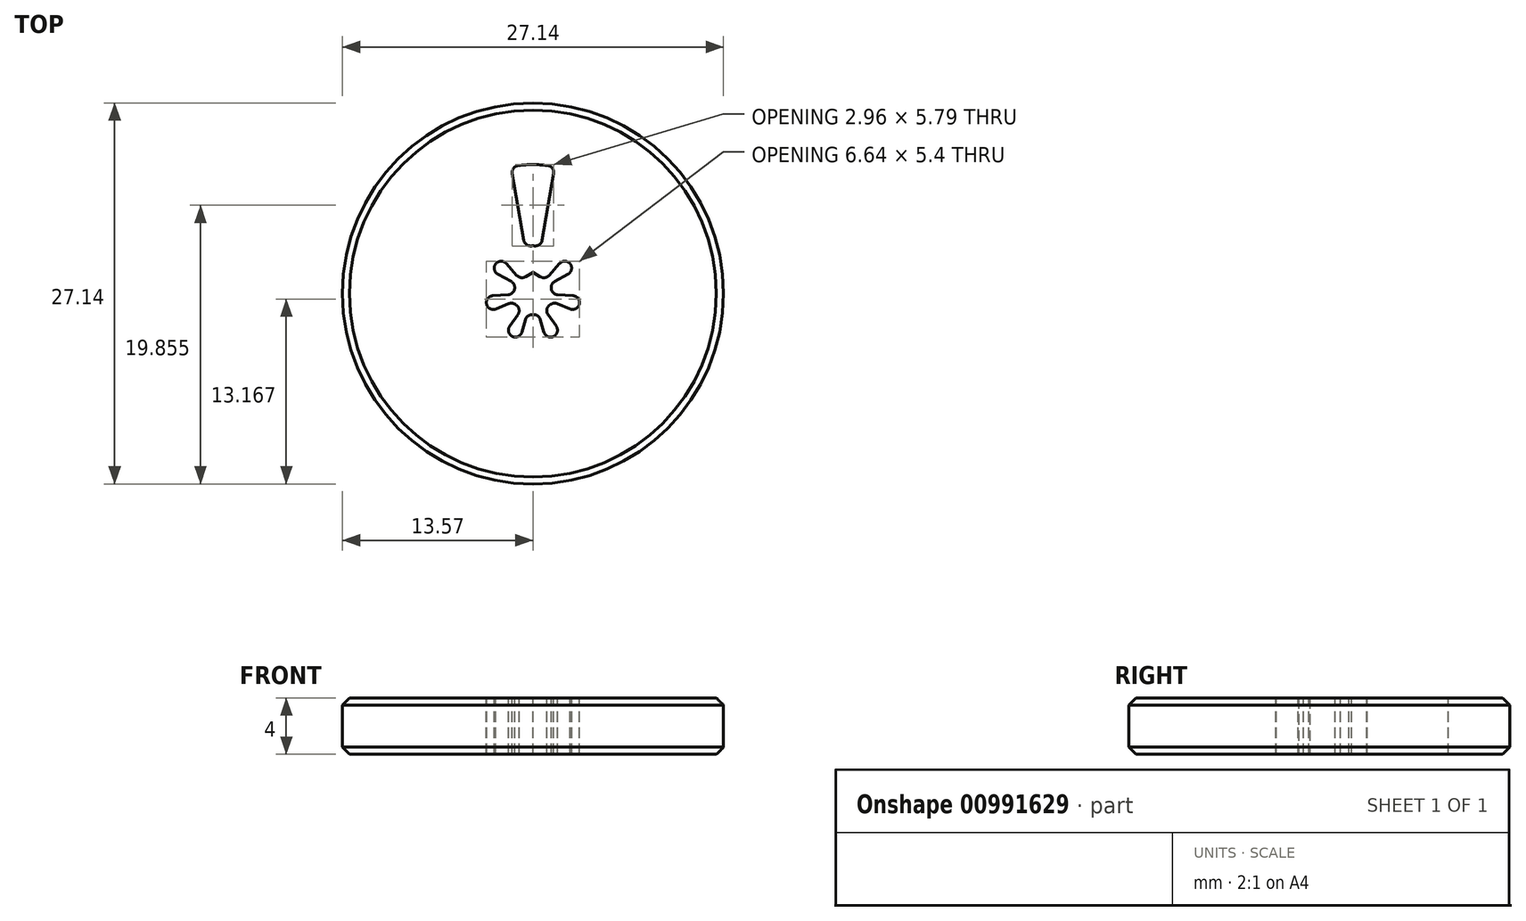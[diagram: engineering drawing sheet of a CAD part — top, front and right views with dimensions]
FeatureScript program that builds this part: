
annotation { "Feature Type Name" : "Feature", "Feature Type Description" : "" }
export const myFeature = defineFeature(function(context is Context, id is Id, definition is map)
    precondition{}
    {
        {
            var Q0;
            Q0=qCreatedBy(makeId("Top.planeOp"),FACE);
            var sketch = newSketch(context, id + "F0", { "sketchPlane" : qUnion([Q0])});
            skCircle(sketch, "E0", {"center": v(0, 0) * mm, "radius": 13.57 * mm});
            skSolve(sketch);
        }
        {
            var Q0;
            Q0=makeQuery(id+"F0.imprint","IMPRINT",FACE,{"disambiguationData":[TD([[makeQuery(id+"F0.imprint","IMPRINT",EDGE,{"derivedFrom":sQuery(id+"F0.wireOp",EDGE,"E0")}),1.0]])]});
            extrude(context, id + "F1", {"entities" : qUnion([Q0]), "endBound" : BoundingType.SYMMETRIC, "depth" : 34 * mm, "offsetDistance" : 25 * mm});
        }
        {
            var Q0;
            Q0=qCreatedBy(makeId("Top.planeOp"),FACE);
            var sketch = newSketch(context, id + "F2", { "sketchPlane" : qUnion([Q0])});
            skPoint(sketch, "E1", {"position": v(0, 17.57) * mm});
            skPoint(sketch, "E2", {"position": v(15.3, 12.2) * mm});
            skPoint(sketch, "E3", {"position": v(19.08, -4.36) * mm});
            skPoint(sketch, "E4", {"position": v(8.5, -17.64) * mm});
            skPoint(sketch, "E5", {"position": v(-8.5, -17.64) * mm});
            skPoint(sketch, "E6", {"position": v(-19.08, -4.36) * mm});
            skPoint(sketch, "E7", {"position": v(-15.3, 12.2) * mm});
            skArc(sketch, "E8", {"start": v(-1, 17.55) * mm, "mid": v(0, 17.57) * mm, "end": v(1, 17.55) * mm});
            skPoint(sketch, "E9", {"position": v(-12.18, 9.71) * mm});
            skPoint(sketch, "E10", {"position": v(12.18, 9.71) * mm});
            skPoint(sketch, "E11", {"position": v(15.18, -3.47) * mm});
            skPoint(sketch, "E12", {"position": v(6.76, -14.03) * mm});
            skPoint(sketch, "E13", {"position": v(-6.76, -14.03) * mm});
            skPoint(sketch, "E14", {"position": v(-15.18, -3.47) * mm});
            skPoint(sketch, "E15", {"position": v(0, 13.57) * mm});
            skArc(sketch, "E16", {"start": v(-2.5, 13.34) * mm, "mid": v(0, 13.57) * mm, "end": v(2.5, 13.34) * mm});
            skLineSegment(sketch, "E17", {"start": v(-2.5, 13.34) * mm, "end": v(-1, 17.55) * mm});
            skLineSegment(sketch, "E18", {"start": v(1, 17.55) * mm, "end": v(2.5, 13.34) * mm});
            skLineSegment(sketch, "E19.1.0", {"start": v(14.34, 10.16) * mm, "end": v(11.99, 6.36) * mm});
            skArc(sketch, "E19.1.1", {"start": v(8.87, 10.27) * mm, "mid": v(10.61, 8.46) * mm, "end": v(11.99, 6.36) * mm});
            skLineSegment(sketch, "E19.1.2", {"start": v(8.87, 10.27) * mm, "end": v(13.1, 11.72) * mm});
            skArc(sketch, "E19.1.3", {"start": v(13.1, 11.72) * mm, "mid": v(13.74, 10.96) * mm, "end": v(14.34, 10.16) * mm});
            skLineSegment(sketch, "E19.2.0", {"start": v(16.88, -4.88) * mm, "end": v(12.45, -5.4) * mm});
            skArc(sketch, "E19.2.1", {"start": v(13.56, -0.53) * mm, "mid": v(13.23, -3.02) * mm, "end": v(12.45, -5.4) * mm});
            skLineSegment(sketch, "E19.2.2", {"start": v(13.56, -0.53) * mm, "end": v(17.33, -2.93) * mm});
            skArc(sketch, "E19.2.3", {"start": v(17.33, -2.93) * mm, "mid": v(17.13, -3.91) * mm, "end": v(16.88, -4.88) * mm});
            skLineSegment(sketch, "E19.3.0", {"start": v(6.71, -16.24) * mm, "end": v(3.54, -13.1) * mm});
            skArc(sketch, "E19.3.1", {"start": v(8.04, -10.94) * mm, "mid": v(5.89, -12.23) * mm, "end": v(3.54, -13.1) * mm});
            skLineSegment(sketch, "E19.3.2", {"start": v(8.04, -10.94) * mm, "end": v(8.51, -15.37) * mm});
            skArc(sketch, "E19.3.3", {"start": v(8.51, -15.37) * mm, "mid": v(7.63, -15.83) * mm, "end": v(6.71, -16.24) * mm});
            skLineSegment(sketch, "E19.4.0", {"start": v(-8.51, -15.37) * mm, "end": v(-8.04, -10.94) * mm});
            skArc(sketch, "E19.4.1", {"start": v(-3.54, -13.1) * mm, "mid": v(-5.89, -12.23) * mm, "end": v(-8.04, -10.94) * mm});
            skLineSegment(sketch, "E19.4.2", {"start": v(-3.54, -13.1) * mm, "end": v(-6.71, -16.24) * mm});
            skArc(sketch, "E19.4.3", {"start": v(-6.71, -16.24) * mm, "mid": v(-7.63, -15.83) * mm, "end": v(-8.51, -15.37) * mm});
            skLineSegment(sketch, "E19.5.0", {"start": v(-17.33, -2.93) * mm, "end": v(-13.56, -0.53) * mm});
            skArc(sketch, "E19.5.1", {"start": v(-12.45, -5.4) * mm, "mid": v(-13.23, -3.02) * mm, "end": v(-13.56, -0.53) * mm});
            skLineSegment(sketch, "E19.5.2", {"start": v(-12.45, -5.4) * mm, "end": v(-16.88, -4.88) * mm});
            skArc(sketch, "E19.5.3", {"start": v(-16.88, -4.88) * mm, "mid": v(-17.13, -3.91) * mm, "end": v(-17.33, -2.93) * mm});
            skLineSegment(sketch, "E19.6.0", {"start": v(-13.1, 11.72) * mm, "end": v(-8.87, 10.27) * mm});
            skArc(sketch, "E19.6.1", {"start": v(-11.99, 6.36) * mm, "mid": v(-10.61, 8.46) * mm, "end": v(-8.87, 10.27) * mm});
            skLineSegment(sketch, "E19.6.2", {"start": v(-11.99, 6.36) * mm, "end": v(-14.34, 10.16) * mm});
            skArc(sketch, "E19.6.3", {"start": v(-14.34, 10.16) * mm, "mid": v(-13.74, 10.96) * mm, "end": v(-13.1, 11.72) * mm});
            skLineSegment(sketch, "E19.anchor1", {"start": v(0, 0) * mm, "end": v(2.5, 13.34) * mm, "construction": true});
            skLineSegment(sketch, "E19.anchor2", {"start": v(0, 0) * mm, "end": v(-8.87, 10.27) * mm, "construction": true});
            skSolve(sketch);
        }
        {
            var Q0;
            Q0=makeQuery(id+"F2.imprint","IMPRINT",FACE,{"disambiguationData":[TD([[makeQuery(id+"F2.imprint","IMPRINT",EDGE,{"derivedFrom":sQuery(id+"F2.wireOp",EDGE,"E19.6.0")}),-1.0]])]});
            var Q1;
            Q1=makeQuery(id+"F2.imprint","IMPRINT",FACE,{"disambiguationData":[TD([[makeQuery(id+"F2.imprint","IMPRINT",EDGE,{"derivedFrom":sQuery(id+"F2.wireOp",EDGE,"E8")}),-1.0]])]});
            var Q2;
            Q2=makeQuery(id+"F2.imprint","IMPRINT",FACE,{"disambiguationData":[TD([[makeQuery(id+"F2.imprint","IMPRINT",EDGE,{"derivedFrom":sQuery(id+"F2.wireOp",EDGE,"E19.1.0")}),-1.0]])]});
            var Q3;
            Q3=makeQuery(id+"F2.imprint","IMPRINT",FACE,{"disambiguationData":[TD([[makeQuery(id+"F2.imprint","IMPRINT",EDGE,{"derivedFrom":sQuery(id+"F2.wireOp",EDGE,"E19.2.0")}),-1.0]])]});
            var Q4;
            Q4=makeQuery(id+"F2.imprint","IMPRINT",FACE,{"disambiguationData":[TD([[makeQuery(id+"F2.imprint","IMPRINT",EDGE,{"derivedFrom":sQuery(id+"F2.wireOp",EDGE,"E19.3.0")}),-1.0]])]});
            var Q5;
            Q5=makeQuery(id+"F2.imprint","IMPRINT",FACE,{"disambiguationData":[TD([[makeQuery(id+"F2.imprint","IMPRINT",EDGE,{"derivedFrom":sQuery(id+"F2.wireOp",EDGE,"E19.4.0")}),-1.0]])]});
            var Q6;
            Q6=makeQuery(id+"F2.imprint","IMPRINT",FACE,{"disambiguationData":[TD([[makeQuery(id+"F2.imprint","IMPRINT",EDGE,{"derivedFrom":sQuery(id+"F2.wireOp",EDGE,"E19.5.0")}),-1.0]])]});
            extrude(context, id + "F3", {"entities" : qUnion([Q0, Q1, Q2, Q3, Q4, Q5, Q6]), "operationType" : NewBodyOperationType.ADD, "endBound" : BoundingType.SYMMETRIC, "depth" : 3 * mm, "offsetDistance" : 25 * mm});
        }
        {
            var Q0;
            Q0=makeQuery(id+"F1.opExtrude","CAP_FACE",FACE,{"disambiguationData":[OSD([sQuery(id+"F0.wireOp",EDGE,"E0")])],"isStart":false});
            var sketch = newSketch(context, id + "F4", { "sketchPlane" : qUnion([Q0])});
            skLineSegment(sketch, "E20", {"start": v(0, 0) * mm, "end": v(0, 3.4) * mm});
            skLineSegment(sketch, "E21", {"start": v(0, 3.4) * mm, "end": v(0, 6.79) * mm});
            skLineSegment(sketch, "E22", {"start": v(0, 10.18) * mm, "end": v(0, 13.57) * mm});
            skArc(sketch, "E23", {"start": v(-0.58, 3.34) * mm, "mid": v(0, 3.4) * mm, "end": v(0.58, 3.34) * mm});
            skPoint(sketch, "E24", {"position": v(0, 3.4) * mm});
            skLineSegment(sketch, "E25", {"start": v(0, 0) * mm, "end": v(-1.56, 9.05) * mm});
            skLineSegment(sketch, "E26", {"start": v(1.56, 9.05) * mm, "end": v(0, 0) * mm});
            skCircle(sketch, "E27.cCircle", {"center": v(0, 0) * mm, "radius": 1.5 * mm, "construction": true});
            skLineSegment(sketch, "E27.0", {"start": v(0, 1.5) * mm, "end": v(1.3, 0.75) * mm});
            skLineSegment(sketch, "E27.1", {"start": v(1.3, 0.75) * mm, "end": v(1.3, -0.75) * mm});
            skLineSegment(sketch, "E27.2", {"start": v(1.3, -0.75) * mm, "end": v(0, -1.5) * mm});
            skLineSegment(sketch, "E27.3", {"start": v(0, -1.5) * mm, "end": v(-1.3, -0.75) * mm});
            skLineSegment(sketch, "E27.4", {"start": v(-1.3, -0.75) * mm, "end": v(-1.3, 0.75) * mm});
            skLineSegment(sketch, "E27.5", {"start": v(-1.3, 0.75) * mm, "end": v(0, 1.5) * mm});
            skArc(sketch, "E28", {"start": v(-1.56, 9.05) * mm, "mid": v(0, 9.18) * mm, "end": v(1.56, 9.05) * mm});
            skLineSegment(sketch, "E29", {"start": v(0, 6.79) * mm, "end": v(0, 10.18) * mm});
            skLineSegment(sketch, "E30.1.0", {"start": v(0, 0) * mm, "end": v(-8.05, 4.42) * mm});
            skLineSegment(sketch, "E30.1.1", {"start": v(-6.1, 6.86) * mm, "end": v(0, 0) * mm});
            skArc(sketch, "E30.1.2", {"start": v(-2.97, 1.63) * mm, "mid": v(-2.65, 2.12) * mm, "end": v(-2.25, 2.54) * mm});
            skArc(sketch, "E30.1.3", {"start": v(-8.05, 4.42) * mm, "mid": v(-7.18, 5.72) * mm, "end": v(-6.1, 6.86) * mm});
            skLineSegment(sketch, "E30.2.0", {"start": v(0, 0) * mm, "end": v(-8.47, -3.54) * mm});
            skLineSegment(sketch, "E30.2.1", {"start": v(-9.17, -0.49) * mm, "end": v(0, 0) * mm});
            skArc(sketch, "E30.2.2", {"start": v(-3.13, -1.3) * mm, "mid": v(-3.3, -0.76) * mm, "end": v(-3.39, -0.18) * mm});
            skArc(sketch, "E30.2.3", {"start": v(-8.47, -3.54) * mm, "mid": v(-8.95, -2.04) * mm, "end": v(-9.17, -0.49) * mm});
            skLineSegment(sketch, "E30.3.0", {"start": v(0, 0) * mm, "end": v(-2.52, -8.83) * mm});
            skLineSegment(sketch, "E30.3.1", {"start": v(-5.33, -7.47) * mm, "end": v(0, 0) * mm});
            skArc(sketch, "E30.3.2", {"start": v(-0.93, -3.26) * mm, "mid": v(-1.47, -3.06) * mm, "end": v(-1.97, -2.76) * mm});
            skArc(sketch, "E30.3.3", {"start": v(-2.52, -8.83) * mm, "mid": v(-3.98, -8.27) * mm, "end": v(-5.33, -7.47) * mm});
            skLineSegment(sketch, "E30.4.0", {"start": v(0, 0) * mm, "end": v(5.33, -7.47) * mm});
            skLineSegment(sketch, "E30.4.1", {"start": v(2.52, -8.83) * mm, "end": v(0, 0) * mm});
            skArc(sketch, "E30.4.2", {"start": v(1.97, -2.76) * mm, "mid": v(1.47, -3.06) * mm, "end": v(0.93, -3.26) * mm});
            skArc(sketch, "E30.4.3", {"start": v(5.33, -7.47) * mm, "mid": v(3.98, -8.27) * mm, "end": v(2.52, -8.83) * mm});
            skLineSegment(sketch, "E30.5.0", {"start": v(0, 0) * mm, "end": v(9.17, -0.49) * mm});
            skLineSegment(sketch, "E30.5.1", {"start": v(8.47, -3.54) * mm, "end": v(0, 0) * mm});
            skArc(sketch, "E30.5.2", {"start": v(3.39, -0.18) * mm, "mid": v(3.3, -0.76) * mm, "end": v(3.13, -1.3) * mm});
            skArc(sketch, "E30.5.3", {"start": v(9.17, -0.49) * mm, "mid": v(8.95, -2.04) * mm, "end": v(8.47, -3.54) * mm});
            skLineSegment(sketch, "E30.6.0", {"start": v(0, 0) * mm, "end": v(6.1, 6.86) * mm});
            skLineSegment(sketch, "E30.6.1", {"start": v(8.05, 4.42) * mm, "end": v(0, 0) * mm});
            skArc(sketch, "E30.6.2", {"start": v(2.25, 2.54) * mm, "mid": v(2.65, 2.12) * mm, "end": v(2.97, 1.63) * mm});
            skArc(sketch, "E30.6.3", {"start": v(6.1, 6.86) * mm, "mid": v(7.18, 5.72) * mm, "end": v(8.05, 4.42) * mm});
            skSolve(sketch);
        }
        {
            var Q0;
            {var subQ0=sQuery(id+"F4.wireOp",EDGE,"4e22676c-9bee-4e88-9cae-636ff35edcea.1.0");Q0=makeQuery(id+"F4.imprint","IMPRINT",FACE,{"disambiguationData":[TD([[makeQuery(id+"F4.imprint","IMPRINT",EDGE,{"derivedFrom":subQ0}),-1.0]])]});}
            var Q1;
            {var subQ1=sQuery(id+"F4.wireOp",EDGE,"E21");Q1=makeQuery(id+"F4.imprint","IMPRINT",FACE,{"disambiguationData":[TD([[makeQuery(id+"F4.imprint","IMPRINT",EDGE,{"derivedFrom":subQ1}),1.0]])]});}
            var Q2;
            {var subQ5=sQuery(id+"F4.wireOp",EDGE,"E21");Q2=makeQuery(id+"F4.imprint","IMPRINT",FACE,{"disambiguationData":[TD([[makeQuery(id+"F4.imprint","IMPRINT",EDGE,{"derivedFrom":subQ5}),-1.0]])]});}
            var Q3;
            {var subQ0=sQuery(id+"F4.wireOp",EDGE,"4e22676c-9bee-4e88-9cae-636ff35edcea.6.0");Q3=makeQuery(id+"F4.imprint","IMPRINT",FACE,{"disambiguationData":[TD([[makeQuery(id+"F4.imprint","IMPRINT",EDGE,{"derivedFrom":subQ0}),-1.0]])]});}
            var Q4;
            {var subQ0=sQuery(id+"F4.wireOp",EDGE,"4e22676c-9bee-4e88-9cae-636ff35edcea.5.0");Q4=makeQuery(id+"F4.imprint","IMPRINT",FACE,{"disambiguationData":[TD([[makeQuery(id+"F4.imprint","IMPRINT",EDGE,{"derivedFrom":subQ0}),-1.0]])]});}
            var Q5;
            {var subQ0=sQuery(id+"F4.wireOp",EDGE,"4e22676c-9bee-4e88-9cae-636ff35edcea.4.0");Q5=makeQuery(id+"F4.imprint","IMPRINT",FACE,{"disambiguationData":[TD([[makeQuery(id+"F4.imprint","IMPRINT",EDGE,{"derivedFrom":subQ0}),-1.0]])]});}
            var Q6;
            {var subQ0=sQuery(id+"F4.wireOp",EDGE,"4e22676c-9bee-4e88-9cae-636ff35edcea.3.0");Q6=makeQuery(id+"F4.imprint","IMPRINT",FACE,{"disambiguationData":[TD([[makeQuery(id+"F4.imprint","IMPRINT",EDGE,{"derivedFrom":subQ0}),-1.0]])]});}
            var Q7;
            {var subQ0=sQuery(id+"F4.wireOp",EDGE,"4e22676c-9bee-4e88-9cae-636ff35edcea.2.0");Q7=makeQuery(id+"F4.imprint","IMPRINT",FACE,{"disambiguationData":[TD([[makeQuery(id+"F4.imprint","IMPRINT",EDGE,{"derivedFrom":subQ0}),-1.0]])]});}
            var Q8;
            {var subQ3=sQuery(id+"F4.wireOp",EDGE,"E27.5");var subQ5=sQuery(id+"F4.wireOp",EDGE,"E27.4");var subQ7=makeQuery(id+"F4.imprint","INTERSECT",VERTEX,{"derivedFrom":[subQ5,subQ3]});Q8=makeQuery(id+"F4.imprint","IMPRINT",FACE,{"disambiguationData":[TD([[makeQuery(id+"F4.imprint","IMPRINT",EDGE,{"disambiguationData":[TD([[subQ7,1.0]])],"derivedFrom":subQ5}),-1.0]])]});}
            var Q9;
            {var subQ1=sQuery(id+"F4.wireOp",EDGE,"E25");var subQ3=sQuery(id+"F4.wireOp",EDGE,"E27.5");var subQ4=makeQuery(id+"F4.imprint","INTERSECT",VERTEX,{"derivedFrom":[subQ1,subQ3]});Q9=makeQuery(id+"F4.imprint","IMPRINT",FACE,{"disambiguationData":[TD([[makeQuery(id+"F4.imprint","IMPRINT",EDGE,{"disambiguationData":[TD([[subQ4,1.0]])],"derivedFrom":subQ3}),-1.0]])]});}
            var Q10;
            {var subQ0=sQuery(id+"F4.wireOp",EDGE,"E25");var subQ3=sQuery(id+"F4.wireOp",EDGE,"E27.5");var subQ5=makeQuery(id+"F4.imprint","INTERSECT",VERTEX,{"derivedFrom":[subQ0,subQ3]});Q10=makeQuery(id+"F4.imprint","IMPRINT",FACE,{"disambiguationData":[TD([[makeQuery(id+"F4.imprint","IMPRINT",EDGE,{"disambiguationData":[TD([[subQ5,-1.0]])],"derivedFrom":subQ3}),-1.0]])]});}
            var Q11;
            {var subQ0=sQuery(id+"F4.wireOp",EDGE,"E26");var subQ3=sQuery(id+"F4.wireOp",EDGE,"E27.0");var subQ5=makeQuery(id+"F4.imprint","INTERSECT",VERTEX,{"derivedFrom":[subQ0,subQ3]});Q11=makeQuery(id+"F4.imprint","IMPRINT",FACE,{"disambiguationData":[TD([[makeQuery(id+"F4.imprint","IMPRINT",EDGE,{"disambiguationData":[TD([[subQ5,1.0]])],"derivedFrom":subQ3}),-1.0]])]});}
            var Q12;
            {var subQ1=sQuery(id+"F4.wireOp",EDGE,"E26");var subQ3=sQuery(id+"F4.wireOp",EDGE,"E27.0");var subQ4=makeQuery(id+"F4.imprint","INTERSECT",VERTEX,{"derivedFrom":[subQ1,subQ3]});Q12=makeQuery(id+"F4.imprint","IMPRINT",FACE,{"disambiguationData":[TD([[makeQuery(id+"F4.imprint","IMPRINT",EDGE,{"disambiguationData":[TD([[subQ4,-1.0]])],"derivedFrom":subQ3}),-1.0]])]});}
            var Q13;
            {var subQ3=sQuery(id+"F4.wireOp",EDGE,"E27.1");var subQ5=sQuery(id+"F4.wireOp",EDGE,"E27.0");var subQ7=makeQuery(id+"F4.imprint","INTERSECT",VERTEX,{"derivedFrom":[subQ5,subQ3]});Q13=makeQuery(id+"F4.imprint","IMPRINT",FACE,{"disambiguationData":[TD([[makeQuery(id+"F4.imprint","IMPRINT",EDGE,{"disambiguationData":[TD([[subQ7,1.0]])],"derivedFrom":subQ5}),-1.0]])]});}
            var Q14;
            {var subQ1=sQuery(id+"F4.wireOp",EDGE,"4e22676c-9bee-4e88-9cae-636ff35edcea.5.3");var subQ3=sQuery(id+"F4.wireOp",EDGE,"E27.1");var subQ4=makeQuery(id+"F4.imprint","INTERSECT",VERTEX,{"derivedFrom":[subQ1,subQ3]});Q14=makeQuery(id+"F4.imprint","IMPRINT",FACE,{"disambiguationData":[TD([[makeQuery(id+"F4.imprint","IMPRINT",EDGE,{"disambiguationData":[TD([[subQ4,1.0]])],"derivedFrom":subQ3}),-1.0]])]});}
            var Q15;
            {var subQ1=sQuery(id+"F4.wireOp",EDGE,"4e22676c-9bee-4e88-9cae-636ff35edcea.5.1");var subQ3=sQuery(id+"F4.wireOp",EDGE,"E27.1");var subQ4=makeQuery(id+"F4.imprint","INTERSECT",VERTEX,{"derivedFrom":[subQ1,subQ3]});Q15=makeQuery(id+"F4.imprint","IMPRINT",FACE,{"disambiguationData":[TD([[makeQuery(id+"F4.imprint","IMPRINT",EDGE,{"disambiguationData":[TD([[subQ4,1.0]])],"derivedFrom":subQ3}),-1.0]])]});}
            var Q16;
            {var subQ3=sQuery(id+"F4.wireOp",EDGE,"E27.2");var subQ5=sQuery(id+"F4.wireOp",EDGE,"E27.1");var subQ6=makeQuery(id+"F4.imprint","INTERSECT",VERTEX,{"derivedFrom":[subQ5,subQ3]});Q16=makeQuery(id+"F4.imprint","IMPRINT",FACE,{"disambiguationData":[TD([[makeQuery(id+"F4.imprint","IMPRINT",EDGE,{"disambiguationData":[TD([[subQ6,1.0]])],"derivedFrom":subQ5}),-1.0]])]});}
            var Q17;
            {var subQ1=sQuery(id+"F4.wireOp",EDGE,"4e22676c-9bee-4e88-9cae-636ff35edcea.4.1");var subQ3=sQuery(id+"F4.wireOp",EDGE,"E27.2");var subQ4=makeQuery(id+"F4.imprint","INTERSECT",VERTEX,{"derivedFrom":[subQ1,subQ3]});Q17=makeQuery(id+"F4.imprint","IMPRINT",FACE,{"disambiguationData":[TD([[makeQuery(id+"F4.imprint","IMPRINT",EDGE,{"disambiguationData":[TD([[subQ4,1.0]])],"derivedFrom":subQ3}),-1.0]])]});}
            var Q18;
            {var subQ3=sQuery(id+"F4.wireOp",EDGE,"E27.3");var subQ5=sQuery(id+"F4.wireOp",EDGE,"E27.2");var subQ7=makeQuery(id+"F4.imprint","INTERSECT",VERTEX,{"derivedFrom":[subQ5,subQ3]});Q18=makeQuery(id+"F4.imprint","IMPRINT",FACE,{"disambiguationData":[TD([[makeQuery(id+"F4.imprint","IMPRINT",EDGE,{"disambiguationData":[TD([[subQ7,1.0]])],"derivedFrom":subQ5}),-1.0]])]});}
            var Q19;
            {var subQ1=sQuery(id+"F4.wireOp",EDGE,"4e22676c-9bee-4e88-9cae-636ff35edcea.3.1");var subQ3=sQuery(id+"F4.wireOp",EDGE,"E27.3");var subQ4=makeQuery(id+"F4.imprint","INTERSECT",VERTEX,{"derivedFrom":[subQ1,subQ3]});Q19=makeQuery(id+"F4.imprint","IMPRINT",FACE,{"disambiguationData":[TD([[makeQuery(id+"F4.imprint","IMPRINT",EDGE,{"disambiguationData":[TD([[subQ4,1.0]])],"derivedFrom":subQ3}),-1.0]])]});}
            var Q20;
            {var subQ3=sQuery(id+"F4.wireOp",EDGE,"E27.4");var subQ5=sQuery(id+"F4.wireOp",EDGE,"E27.3");var subQ7=makeQuery(id+"F4.imprint","INTERSECT",VERTEX,{"derivedFrom":[subQ5,subQ3]});Q20=makeQuery(id+"F4.imprint","IMPRINT",FACE,{"disambiguationData":[TD([[makeQuery(id+"F4.imprint","IMPRINT",EDGE,{"disambiguationData":[TD([[subQ7,1.0]])],"derivedFrom":subQ5}),-1.0]])]});}
            var Q21;
            {var subQ1=sQuery(id+"F4.wireOp",EDGE,"4e22676c-9bee-4e88-9cae-636ff35edcea.2.1");var subQ3=sQuery(id+"F4.wireOp",EDGE,"E27.4");var subQ4=makeQuery(id+"F4.imprint","INTERSECT",VERTEX,{"derivedFrom":[subQ1,subQ3]});Q21=makeQuery(id+"F4.imprint","IMPRINT",FACE,{"disambiguationData":[TD([[makeQuery(id+"F4.imprint","IMPRINT",EDGE,{"disambiguationData":[TD([[subQ4,1.0]])],"derivedFrom":subQ3}),-1.0]])]});}
            var Q22;
            {var subQ1=sQuery(id+"F4.wireOp",EDGE,"4e22676c-9bee-4e88-9cae-636ff35edcea.1.3");var subQ3=sQuery(id+"F4.wireOp",EDGE,"E27.4");var subQ4=makeQuery(id+"F4.imprint","INTERSECT",VERTEX,{"derivedFrom":[subQ1,subQ3]});Q22=makeQuery(id+"F4.imprint","IMPRINT",FACE,{"disambiguationData":[TD([[makeQuery(id+"F4.imprint","IMPRINT",EDGE,{"disambiguationData":[TD([[subQ4,1.0]])],"derivedFrom":subQ3}),-1.0]])]});}
            var Q23;
            {var subQ2=sQuery(id+"F4.wireOp",EDGE,"E30.1.2");Q23=makeQuery(id+"F4.imprint","IMPRINT",FACE,{"disambiguationData":[TD([[makeQuery(id+"F4.imprint","IMPRINT",EDGE,{"derivedFrom":subQ2}),1.0]])]});}
            var Q24;
            {var subQ2=sQuery(id+"F4.wireOp",EDGE,"E30.6.2");Q24=makeQuery(id+"F4.imprint","IMPRINT",FACE,{"disambiguationData":[TD([[makeQuery(id+"F4.imprint","IMPRINT",EDGE,{"derivedFrom":subQ2}),1.0]])]});}
            var Q25;
            {var subQ2=sQuery(id+"F4.wireOp",EDGE,"E30.5.2");Q25=makeQuery(id+"F4.imprint","IMPRINT",FACE,{"disambiguationData":[TD([[makeQuery(id+"F4.imprint","IMPRINT",EDGE,{"derivedFrom":subQ2}),1.0]])]});}
            var Q26;
            {var subQ2=sQuery(id+"F4.wireOp",EDGE,"E30.2.2");Q26=makeQuery(id+"F4.imprint","IMPRINT",FACE,{"disambiguationData":[TD([[makeQuery(id+"F4.imprint","IMPRINT",EDGE,{"derivedFrom":subQ2}),1.0]])]});}
            var Q27;
            {var subQ2=sQuery(id+"F4.wireOp",EDGE,"E30.3.2");Q27=makeQuery(id+"F4.imprint","IMPRINT",FACE,{"disambiguationData":[TD([[makeQuery(id+"F4.imprint","IMPRINT",EDGE,{"derivedFrom":subQ2}),1.0]])]});}
            var Q28;
            {var subQ2=sQuery(id+"F4.wireOp",EDGE,"E30.4.2");Q28=makeQuery(id+"F4.imprint","IMPRINT",FACE,{"disambiguationData":[TD([[makeQuery(id+"F4.imprint","IMPRINT",EDGE,{"derivedFrom":subQ2}),1.0]])]});}
            extrude(context, id + "F5", {"entities" : qUnion([Q0, Q1, Q2, Q3, Q4, Q5, Q6, Q7, Q8, Q9, Q10, Q11, Q12, Q13, Q14, Q15, Q16, Q17, Q18, Q19, Q20, Q21, Q22, Q23, Q24, Q25, Q26, Q27, Q28]), "operationType" : NewBodyOperationType.REMOVE, "oppositeDirection" : true, "depth" : 34 * mm, "offsetDistance" : 25 * mm});
        }
        {
            var Q0;
            Q0=makeQuery(id+"F1.opExtrude","CAP_FACE",FACE,{"disambiguationData":[OSD([sQuery(id+"F0.wireOp",EDGE,"E0")])],"isStart":true});
            var sketch = newSketch(context, id + "F6", { "sketchPlane" : qUnion([Q0])});
            skCircle(sketch, "E31", {"center": v(0, 0) * mm, "radius": 13.57 * mm});
            skCircle(sketch, "E32", {"center": v(0, 0) * mm, "radius": 15.57 * mm});
            skSolve(sketch);
        }
        {
            var Q0;
            Q0=qSketchRegion(id+"F6",true);
            extrude(context, id + "F7", {"entities" : qUnion([Q0]), "operationType" : NewBodyOperationType.ADD, "oppositeDirection" : true, "depth" : 1.5 * mm, "offsetDistance" : 25 * mm});
        }
        {
            var Q0;
            Q0=makeQuery(id+"F7.opExtrude","CAP_EDGE",EDGE,{"disambiguationData":[OSD([sQuery(id+"F6.wireOp",EDGE,"E32")])],"isStart":false});
            chamfer(context, id + "F8", {"entities" : qUnion([Q0]), "chamferType" : ChamferType.TWO_OFFSETS, "width1" : 2 * mm, "oppositeDirection" : true, "width2" : 1 * mm, "tangentPropagation" : true});
        }
        {
            var Q0;
            Q0=makeQuery(id+"F3.opExtrude","SWEPT_EDGE",EDGE,{"disambiguationData":[OSD([sQuery(id+"F2.wireOp",EDGE,"E19.1.0"),sQuery(id+"F2.wireOp",EDGE,"E19.1.3")])]});
            var Q1;
            Q1=makeQuery(id+"F3.opExtrude","SWEPT_EDGE",EDGE,{"disambiguationData":[OSD([sQuery(id+"F2.wireOp",EDGE,"E19.1.2"),sQuery(id+"F2.wireOp",EDGE,"E19.1.3")])]});
            var Q2;
            Q2=makeQuery(id+"F3.opExtrude","SWEPT_EDGE",EDGE,{"disambiguationData":[OSD([sQuery(id+"F2.wireOp",EDGE,"E8"),sQuery(id+"F2.wireOp",EDGE,"E18")])]});
            var Q3;
            Q3=makeQuery(id+"F3.opExtrude","SWEPT_EDGE",EDGE,{"disambiguationData":[OSD([sQuery(id+"F2.wireOp",EDGE,"E8"),sQuery(id+"F2.wireOp",EDGE,"E17")])]});
            var Q4;
            Q4=makeQuery(id+"F3.opExtrude","SWEPT_EDGE",EDGE,{"disambiguationData":[OSD([sQuery(id+"F2.wireOp",EDGE,"E19.6.0"),sQuery(id+"F2.wireOp",EDGE,"E19.6.3")])]});
            var Q5;
            Q5=makeQuery(id+"F3.opExtrude","SWEPT_EDGE",EDGE,{"disambiguationData":[OSD([sQuery(id+"F2.wireOp",EDGE,"E19.6.2"),sQuery(id+"F2.wireOp",EDGE,"E19.6.3")])]});
            var Q6;
            Q6=makeQuery(id+"F3.opExtrude","SWEPT_EDGE",EDGE,{"disambiguationData":[OSD([sQuery(id+"F2.wireOp",EDGE,"E19.5.0"),sQuery(id+"F2.wireOp",EDGE,"E19.5.3")])]});
            var Q7;
            Q7=makeQuery(id+"F3.opExtrude","SWEPT_EDGE",EDGE,{"disambiguationData":[OSD([sQuery(id+"F2.wireOp",EDGE,"E19.5.2"),sQuery(id+"F2.wireOp",EDGE,"E19.5.3")])]});
            var Q8;
            Q8=makeQuery(id+"F3.opExtrude","SWEPT_EDGE",EDGE,{"disambiguationData":[OSD([sQuery(id+"F2.wireOp",EDGE,"E19.4.0"),sQuery(id+"F2.wireOp",EDGE,"E19.4.3")])]});
            var Q9;
            Q9=makeQuery(id+"F3.opExtrude","SWEPT_EDGE",EDGE,{"disambiguationData":[OSD([sQuery(id+"F2.wireOp",EDGE,"E19.4.2"),sQuery(id+"F2.wireOp",EDGE,"E19.4.3")])]});
            var Q10;
            Q10=makeQuery(id+"F3.opExtrude","SWEPT_EDGE",EDGE,{"disambiguationData":[OSD([sQuery(id+"F2.wireOp",EDGE,"E19.3.0"),sQuery(id+"F2.wireOp",EDGE,"E19.3.3")])]});
            var Q11;
            Q11=makeQuery(id+"F3.opExtrude","SWEPT_EDGE",EDGE,{"disambiguationData":[OSD([sQuery(id+"F2.wireOp",EDGE,"E19.3.2"),sQuery(id+"F2.wireOp",EDGE,"E19.3.3")])]});
            var Q12;
            Q12=makeQuery(id+"F3.opExtrude","SWEPT_EDGE",EDGE,{"disambiguationData":[OSD([sQuery(id+"F2.wireOp",EDGE,"E19.2.0"),sQuery(id+"F2.wireOp",EDGE,"E19.2.3")])]});
            var Q13;
            Q13=makeQuery(id+"F3.opExtrude","SWEPT_EDGE",EDGE,{"disambiguationData":[OSD([sQuery(id+"F2.wireOp",EDGE,"E19.2.2"),sQuery(id+"F2.wireOp",EDGE,"E19.2.3")])]});
            fillet(context, id + "F9", {"entities" : qUnion([Q0, Q1, Q2, Q3, Q4, Q5, Q6, Q7, Q8, Q9, Q10, Q11, Q12, Q13]), "radius" : 1 * mm, "tangentPropagation" : true, "allowEdgeOverflow" : false});
        }
        {
            var Q0;
            Q0=makeQuery(id+"F7.boolean.opBoolean","MERGE",FACE,{"derivedFrom":[makeQuery(id+"F1.opExtrude","CAP_FACE",FACE,{"disambiguationData":[OSD([sQuery(id+"F0.wireOp",EDGE,"E0")])],"isStart":true}),makeQuery(id+"F7.opExtrude","CAP_FACE",FACE,{"disambiguationData":[OSD([sQuery(id+"F6.wireOp",EDGE,"E31"),sQuery(id+"F6.wireOp",EDGE,"E32")])],"isStart":true})]});
            var sketch = newSketch(context, id + "F10", { "sketchPlane" : qUnion([Q0])});
            skCircle(sketch, "E33", {"center": v(0, 0) * mm, "radius": 13.57 * mm});
            skCircle(sketch, "E34", {"center": v(0, 0) * mm, "radius": 10.32 * mm});
            skSolve(sketch);
        }
        {
            var Q0;
            Q0=makeQuery(id+"F3.opExtrude","CAP_FACE",FACE,{"disambiguationData":[OSD([sQuery(id+"F2.wireOp",EDGE,"E19.5.0"),sQuery(id+"F2.wireOp",EDGE,"E19.5.1"),sQuery(id+"F2.wireOp",EDGE,"E19.5.2"),sQuery(id+"F2.wireOp",EDGE,"E19.5.3")])],"isStart":false});
            cPlane(context, id + "F11", {"entities" : qUnion([Q0]), "cplaneType" : CPlaneType.OFFSET, "offset" : 0.5 * mm, "width" : 150 * mm, "height" : 150 * mm});
        }
        {
            var Q0;
            Q0=qCreatedBy(id+"F11.planeOp",FACE);
            var sketch = newSketch(context, id + "F12", { "sketchPlane" : qUnion([Q0])});
            skCircle(sketch, "E35", {"center": v(0, 0) * mm, "radius": 13.57 * mm});
            skCircle(sketch, "E36", {"center": v(0, 0) * mm, "radius": 10.57 * mm});
            skSolve(sketch);
        }
        {
            var Q0;
            Q0=qSketchRegion(id+"F12",true);
            extrude(context, id + "F13", {"entities" : qUnion([Q0]), "operationType" : NewBodyOperationType.REMOVE, "depth" : 2 * mm, "offsetDistance" : 25 * mm});
        }
        {
            var Q0;
            Q0=makeQuery(id+"F3.opExtrude","CAP_FACE",FACE,{"disambiguationData":[OSD([sQuery(id+"F2.wireOp",EDGE,"E19.4.0"),sQuery(id+"F2.wireOp",EDGE,"E19.4.1"),sQuery(id+"F2.wireOp",EDGE,"E19.4.2"),sQuery(id+"F2.wireOp",EDGE,"E19.4.3")])],"isStart":true});
            cPlane(context, id + "F14", {"entities" : qUnion([Q0]), "cplaneType" : CPlaneType.OFFSET, "offset" : 0.5 * mm, "width" : 150 * mm, "height" : 150 * mm});
        }
        {
            var Q0;
            Q0=qCreatedBy(id+"F14.planeOp",FACE);
            var sketch = newSketch(context, id + "F15", { "sketchPlane" : qUnion([Q0])});
            skCircle(sketch, "E37", {"center": v(0, 0) * mm, "radius": 13.57 * mm});
            skCircle(sketch, "E38", {"center": v(0, 0) * mm, "radius": 10.57 * mm});
            skSolve(sketch);
        }
        {
            var Q0;
            Q0=qSketchRegion(id+"F15",true);
            extrude(context, id + "F16", {"entities" : qUnion([Q0]), "operationType" : NewBodyOperationType.REMOVE, "depth" : 2 * mm, "offsetDistance" : 25 * mm});
        }
        {
            var Q0;
            Q0=makeQuery(id+"F16.boolean.opBoolean","COPY",EDGE,{"derivedFrom":makeQuery(id+"F16.opExtrude","CAP_EDGE",EDGE,{"disambiguationData":[OSD([sQuery(id+"F15.wireOp",EDGE,"E37")])],"isStart":false})});
            var Q1;
            Q1=makeQuery(id+"F16.boolean.opBoolean","COPY",EDGE,{"derivedFrom":makeQuery(id+"F16.opExtrude","CAP_EDGE",EDGE,{"disambiguationData":[OSD([sQuery(id+"F15.wireOp",EDGE,"E37")])],"isStart":true})});
            var Q2;
            Q2=makeQuery(id+"F13.boolean.opBoolean","COPY",EDGE,{"derivedFrom":makeQuery(id+"F13.opExtrude","CAP_EDGE",EDGE,{"disambiguationData":[OSD([sQuery(id+"F12.wireOp",EDGE,"E35")])],"isStart":true})});
            var Q3;
            Q3=makeQuery(id+"F13.boolean.opBoolean","COPY",EDGE,{"derivedFrom":makeQuery(id+"F13.opExtrude","CAP_EDGE",EDGE,{"disambiguationData":[OSD([sQuery(id+"F12.wireOp",EDGE,"E35")])],"isStart":false})});
            chamfer(context, id + "F17", {"entities" : qUnion([Q0, Q1, Q2, Q3]), "width" : 0.5 * mm, "tangentPropagation" : true});
        }
        {
            var Q0;
            Q0=makeQuery(id+"F1.opExtrude","CAP_FACE",FACE,{"disambiguationData":[OSD([sQuery(id+"F0.wireOp",EDGE,"E0")])],"isStart":false});
            var sketch = newSketch(context, id + "F18", { "sketchPlane" : qUnion([Q0])});
            skCircle(sketch, "E39", {"center": v(0, 0) * mm, "radius": 13.57 * mm});
            skCircle(sketch, "E40", {"center": v(0, 0) * mm, "radius": 19.77 * mm});
            skSolve(sketch);
        }
        {
            var Q0;
            Q0=makeQuery(id+"F18.imprint","IMPRINT",FACE,{"disambiguationData":[TD([[makeQuery(id+"F18.imprint","IMPRINT",EDGE,{"derivedFrom":sQuery(id+"F18.wireOp",EDGE,"E39")}),-1.0]])]});
            extrude(context, id + "F19", {"entities" : qUnion([Q0]), "operationType" : NewBodyOperationType.REMOVE, "oppositeDirection" : true, "depth" : 100 * mm, "offsetDistance" : 25 * mm});
        }
        {
            var Q0;
            Q0=makeQuery(id+"F1.opExtrude","CAP_FACE",FACE,{"disambiguationData":[OSD([sQuery(id+"F0.wireOp",EDGE,"E0")])],"isStart":false});
            extrude(context, id + "F20", {"entities" : qUnion([Q0]), "operationType" : NewBodyOperationType.REMOVE, "oppositeDirection" : true, "depth" : 15 * mm, "offsetDistance" : 25 * mm});
        }
        {
            var Q0;
            Q0=makeQuery(id+"F10.imprint","IMPRINT",FACE,{"disambiguationData":[TD([[makeQuery(id+"F10.imprint","IMPRINT",EDGE,{"derivedFrom":sQuery(id+"F10.wireOp",EDGE,"E33")}),1.0]])]});
            var Q1;
            Q1=makeQuery(id+"F10.imprint","IMPRINT",FACE,{"disambiguationData":[TD([[makeQuery(id+"F10.imprint","IMPRINT",EDGE,{"derivedFrom":sQuery(id+"F10.wireOp",EDGE,"E34")}),1.0]])]});
            extrude(context, id + "F21", {"entities" : qUnion([Q0, Q1]), "operationType" : NewBodyOperationType.REMOVE, "oppositeDirection" : true, "depth" : 15 * mm, "offsetDistance" : 25 * mm});
        }
        {
            var Q0;
            Q0=makeQuery(id+"F21.boolean.opBoolean","MERGE",FACE,{"derivedFrom":[makeQuery(id+"F16.boolean.opBoolean","COPY",FACE,{"derivedFrom":makeQuery(id+"F16.opExtrude","CAP_FACE",FACE,{"disambiguationData":[OSD([sQuery(id+"F15.wireOp",EDGE,"E37"),sQuery(id+"F15.wireOp",EDGE,"E38")])],"isStart":true})})],"fromTools":[makeQuery(id+"F21.opExtrude","CAP_FACE",FACE,{"disambiguationData":[OSD([sQuery(id+"F4.wireOp",EDGE,"E23"),sQuery(id+"F4.wireOp",EDGE,"E25"),sQuery(id+"F4.wireOp",EDGE,"E26"),sQuery(id+"F4.wireOp",EDGE,"E27.0"),sQuery(id+"F4.wireOp",EDGE,"E27.1"),sQuery(id+"F4.wireOp",EDGE,"E27.2"),sQuery(id+"F4.wireOp",EDGE,"E27.3"),sQuery(id+"F4.wireOp",EDGE,"E27.4"),sQuery(id+"F4.wireOp",EDGE,"E27.5"),sQuery(id+"F4.wireOp",EDGE,"E28"),sQuery(id+"F4.wireOp",EDGE,"E30.1.0"),sQuery(id+"F4.wireOp",EDGE,"E30.1.1"),sQuery(id+"F4.wireOp",EDGE,"E30.1.2"),sQuery(id+"F4.wireOp",EDGE,"E30.1.3"),sQuery(id+"F4.wireOp",EDGE,"E30.2.0"),sQuery(id+"F4.wireOp",EDGE,"E30.2.1"),sQuery(id+"F4.wireOp",EDGE,"E30.2.2"),sQuery(id+"F4.wireOp",EDGE,"E30.2.3"),sQuery(id+"F4.wireOp",EDGE,"E30.3.0"),sQuery(id+"F4.wireOp",EDGE,"E30.3.1"),sQuery(id+"F4.wireOp",EDGE,"E30.3.2"),sQuery(id+"F4.wireOp",EDGE,"E30.3.3"),sQuery(id+"F4.wireOp",EDGE,"E30.4.0"),sQuery(id+"F4.wireOp",EDGE,"E30.4.1"),sQuery(id+"F4.wireOp",EDGE,"E30.4.2"),sQuery(id+"F4.wireOp",EDGE,"E30.4.3"),sQuery(id+"F4.wireOp",EDGE,"E30.5.0"),sQuery(id+"F4.wireOp",EDGE,"E30.5.1"),sQuery(id+"F4.wireOp",EDGE,"E30.5.2"),sQuery(id+"F4.wireOp",EDGE,"E30.5.3"),sQuery(id+"F4.wireOp",EDGE,"E30.6.0"),sQuery(id+"F4.wireOp",EDGE,"E30.6.1"),sQuery(id+"F4.wireOp",EDGE,"E30.6.2"),sQuery(id+"F4.wireOp",EDGE,"E30.6.3"),sQuery(id+"F10.wireOp",EDGE,"E33")])],"isStart":false})]});
            var sketch = newSketch(context, id + "F22", { "sketchPlane" : qUnion([Q0])});
            skCircle(sketch, "E41", {"center": v(0, 0) * mm, "radius": 2.05 * mm});
            skSolve(sketch);
        }
        {
            var Q0;
            Q0=makeQuery(id+"F22.imprint","IMPRINT",FACE,{"disambiguationData":[TD([[makeQuery(id+"F22.imprint","IMPRINT",EDGE,{"derivedFrom":sQuery(id+"F22.wireOp",EDGE,"E41")}),1.0]])]});
            extrude(context, id + "F23", {"entities" : qUnion([Q0]), "operationType" : NewBodyOperationType.REMOVE, "oppositeDirection" : true, "depth" : 25 * mm, "offsetDistance" : 25 * mm});
        }
        {
            var Q0;
            Q0=makeQuery(id+"F5.boolean.opBoolean","COPY",EDGE,{"derivedFrom":makeQuery(id+"F5.opExtrude","SWEPT_EDGE",EDGE,{"disambiguationData":[OSD([sQuery(id+"F4.wireOp",EDGE,"E30.3.1"),sQuery(id+"F4.wireOp",EDGE,"E30.3.2")])]})});
            var Q1;
            Q1=makeQuery(id+"F5.boolean.opBoolean","COPY",EDGE,{"derivedFrom":makeQuery(id+"F5.opExtrude","SWEPT_EDGE",EDGE,{"disambiguationData":[OSD([sQuery(id+"F4.wireOp",EDGE,"E30.3.0"),sQuery(id+"F4.wireOp",EDGE,"E30.3.2")])]})});
            var Q2;
            Q2=makeQuery(id+"F5.boolean.opBoolean","COPY",EDGE,{"derivedFrom":makeQuery(id+"F5.opExtrude","SWEPT_EDGE",EDGE,{"disambiguationData":[OSD([sQuery(id+"F4.wireOp",EDGE,"E30.4.0"),sQuery(id+"F4.wireOp",EDGE,"E30.4.2")])]})});
            var Q3;
            Q3=makeQuery(id+"F5.boolean.opBoolean","COPY",EDGE,{"derivedFrom":makeQuery(id+"F5.opExtrude","SWEPT_EDGE",EDGE,{"disambiguationData":[OSD([sQuery(id+"F4.wireOp",EDGE,"E30.4.1"),sQuery(id+"F4.wireOp",EDGE,"E30.4.2")])]})});
            var Q4;
            Q4=makeQuery(id+"F5.boolean.opBoolean","COPY",EDGE,{"derivedFrom":makeQuery(id+"F5.opExtrude","SWEPT_EDGE",EDGE,{"disambiguationData":[OSD([sQuery(id+"F4.wireOp",EDGE,"E30.5.0"),sQuery(id+"F4.wireOp",EDGE,"E30.5.2")])]})});
            var Q5;
            Q5=makeQuery(id+"F5.boolean.opBoolean","COPY",EDGE,{"derivedFrom":makeQuery(id+"F5.opExtrude","SWEPT_EDGE",EDGE,{"disambiguationData":[OSD([sQuery(id+"F4.wireOp",EDGE,"E30.5.1"),sQuery(id+"F4.wireOp",EDGE,"E30.5.2")])]})});
            var Q6;
            Q6=makeQuery(id+"F5.boolean.opBoolean","COPY",EDGE,{"derivedFrom":makeQuery(id+"F5.opExtrude","SWEPT_EDGE",EDGE,{"disambiguationData":[OSD([sQuery(id+"F4.wireOp",EDGE,"E30.6.0"),sQuery(id+"F4.wireOp",EDGE,"E30.6.2")])]})});
            var Q7;
            Q7=makeQuery(id+"F5.boolean.opBoolean","COPY",EDGE,{"derivedFrom":makeQuery(id+"F5.opExtrude","SWEPT_EDGE",EDGE,{"disambiguationData":[OSD([sQuery(id+"F4.wireOp",EDGE,"E30.6.1"),sQuery(id+"F4.wireOp",EDGE,"E30.6.2")])]})});
            var Q8;
            Q8=makeQuery(id+"F5.boolean.opBoolean","COPY",EDGE,{"derivedFrom":makeQuery(id+"F5.opExtrude","SWEPT_EDGE",EDGE,{"disambiguationData":[OSD([sQuery(id+"F4.wireOp",EDGE,"E23"),sQuery(id+"F4.wireOp",EDGE,"E25")])]})});
            var Q9;
            Q9=makeQuery(id+"F5.boolean.opBoolean","COPY",EDGE,{"derivedFrom":makeQuery(id+"F5.opExtrude","SWEPT_EDGE",EDGE,{"disambiguationData":[OSD([sQuery(id+"F4.wireOp",EDGE,"E23"),sQuery(id+"F4.wireOp",EDGE,"E26")])]})});
            var Q10;
            Q10=makeQuery(id+"F5.boolean.opBoolean","COPY",EDGE,{"derivedFrom":makeQuery(id+"F5.opExtrude","SWEPT_EDGE",EDGE,{"disambiguationData":[OSD([sQuery(id+"F4.wireOp",EDGE,"E30.1.1"),sQuery(id+"F4.wireOp",EDGE,"E30.1.2")])]})});
            var Q11;
            Q11=makeQuery(id+"F5.boolean.opBoolean","COPY",EDGE,{"derivedFrom":makeQuery(id+"F5.opExtrude","SWEPT_EDGE",EDGE,{"disambiguationData":[OSD([sQuery(id+"F4.wireOp",EDGE,"E30.1.0"),sQuery(id+"F4.wireOp",EDGE,"E30.1.2")])]})});
            var Q12;
            Q12=makeQuery(id+"F5.boolean.opBoolean","COPY",EDGE,{"derivedFrom":makeQuery(id+"F5.opExtrude","SWEPT_EDGE",EDGE,{"disambiguationData":[OSD([sQuery(id+"F4.wireOp",EDGE,"E30.2.1"),sQuery(id+"F4.wireOp",EDGE,"E30.2.2")])]})});
            var Q13;
            Q13=makeQuery(id+"F5.boolean.opBoolean","COPY",EDGE,{"derivedFrom":makeQuery(id+"F5.opExtrude","SWEPT_EDGE",EDGE,{"disambiguationData":[OSD([sQuery(id+"F4.wireOp",EDGE,"E30.2.0"),sQuery(id+"F4.wireOp",EDGE,"E30.2.2")])]})});
            var Q14;
            Q14=makeQuery(id+"F5.boolean.opBoolean","COPY",EDGE,{"derivedFrom":makeQuery(id+"F5.opExtrude","SWEPT_EDGE",EDGE,{"disambiguationData":[OSD([sQuery(id+"F4.wireOp",EDGE,"E30.2.1"),sQuery(id+"F4.wireOp",EDGE,"E30.2.3")])]})});
            var Q15;
            Q15=makeQuery(id+"F5.boolean.opBoolean","COPY",EDGE,{"derivedFrom":makeQuery(id+"F5.opExtrude","SWEPT_EDGE",EDGE,{"disambiguationData":[OSD([sQuery(id+"F4.wireOp",EDGE,"E30.2.0"),sQuery(id+"F4.wireOp",EDGE,"E30.2.3")])]})});
            var Q16;
            Q16=makeQuery(id+"F5.boolean.opBoolean","COPY",EDGE,{"derivedFrom":makeQuery(id+"F5.opExtrude","SWEPT_EDGE",EDGE,{"disambiguationData":[OSD([sQuery(id+"F4.wireOp",EDGE,"E30.1.0"),sQuery(id+"F4.wireOp",EDGE,"E30.1.3")])]})});
            var Q17;
            Q17=makeQuery(id+"F5.boolean.opBoolean","COPY",EDGE,{"derivedFrom":makeQuery(id+"F5.opExtrude","SWEPT_EDGE",EDGE,{"disambiguationData":[OSD([sQuery(id+"F4.wireOp",EDGE,"E30.1.1"),sQuery(id+"F4.wireOp",EDGE,"E30.1.3")])]})});
            var Q18;
            Q18=makeQuery(id+"F5.boolean.opBoolean","COPY",EDGE,{"derivedFrom":makeQuery(id+"F5.opExtrude","SWEPT_EDGE",EDGE,{"disambiguationData":[OSD([sQuery(id+"F4.wireOp",EDGE,"E25"),sQuery(id+"F4.wireOp",EDGE,"E28")])]})});
            var Q19;
            Q19=makeQuery(id+"F5.boolean.opBoolean","COPY",EDGE,{"derivedFrom":makeQuery(id+"F5.opExtrude","SWEPT_EDGE",EDGE,{"disambiguationData":[OSD([sQuery(id+"F4.wireOp",EDGE,"E26"),sQuery(id+"F4.wireOp",EDGE,"E28")])]})});
            var Q20;
            Q20=makeQuery(id+"F5.boolean.opBoolean","COPY",EDGE,{"derivedFrom":makeQuery(id+"F5.opExtrude","SWEPT_EDGE",EDGE,{"disambiguationData":[OSD([sQuery(id+"F4.wireOp",EDGE,"E30.6.0"),sQuery(id+"F4.wireOp",EDGE,"E30.6.3")])]})});
            var Q21;
            Q21=makeQuery(id+"F5.boolean.opBoolean","COPY",EDGE,{"derivedFrom":makeQuery(id+"F5.opExtrude","SWEPT_EDGE",EDGE,{"disambiguationData":[OSD([sQuery(id+"F4.wireOp",EDGE,"E30.6.1"),sQuery(id+"F4.wireOp",EDGE,"E30.6.3")])]})});
            var Q22;
            Q22=makeQuery(id+"F5.boolean.opBoolean","COPY",EDGE,{"derivedFrom":makeQuery(id+"F5.opExtrude","SWEPT_EDGE",EDGE,{"disambiguationData":[OSD([sQuery(id+"F4.wireOp",EDGE,"E30.5.0"),sQuery(id+"F4.wireOp",EDGE,"E30.5.3")])]})});
            var Q23;
            Q23=makeQuery(id+"F5.boolean.opBoolean","COPY",EDGE,{"derivedFrom":makeQuery(id+"F5.opExtrude","SWEPT_EDGE",EDGE,{"disambiguationData":[OSD([sQuery(id+"F4.wireOp",EDGE,"E30.5.1"),sQuery(id+"F4.wireOp",EDGE,"E30.5.3")])]})});
            var Q24;
            Q24=makeQuery(id+"F5.boolean.opBoolean","COPY",EDGE,{"derivedFrom":makeQuery(id+"F5.opExtrude","SWEPT_EDGE",EDGE,{"disambiguationData":[OSD([sQuery(id+"F4.wireOp",EDGE,"E30.4.0"),sQuery(id+"F4.wireOp",EDGE,"E30.4.3")])]})});
            var Q25;
            Q25=makeQuery(id+"F5.boolean.opBoolean","COPY",EDGE,{"derivedFrom":makeQuery(id+"F5.opExtrude","SWEPT_EDGE",EDGE,{"disambiguationData":[OSD([sQuery(id+"F4.wireOp",EDGE,"E30.4.1"),sQuery(id+"F4.wireOp",EDGE,"E30.4.3")])]})});
            var Q26;
            Q26=makeQuery(id+"F5.boolean.opBoolean","COPY",EDGE,{"derivedFrom":makeQuery(id+"F5.opExtrude","SWEPT_EDGE",EDGE,{"disambiguationData":[OSD([sQuery(id+"F4.wireOp",EDGE,"E30.3.0"),sQuery(id+"F4.wireOp",EDGE,"E30.3.3")])]})});
            var Q27;
            Q27=makeQuery(id+"F5.boolean.opBoolean","COPY",EDGE,{"derivedFrom":makeQuery(id+"F5.opExtrude","SWEPT_EDGE",EDGE,{"disambiguationData":[OSD([sQuery(id+"F4.wireOp",EDGE,"E30.3.1"),sQuery(id+"F4.wireOp",EDGE,"E30.3.3")])]})});
            fillet(context, id + "F24", {"entities" : qUnion([Q0, Q1, Q2, Q3, Q4, Q5, Q6, Q7, Q8, Q9, Q10, Q11, Q12, Q13, Q14, Q15, Q16, Q17, Q18, Q19, Q20, Q21, Q22, Q23, Q24, Q25, Q26, Q27]), "radius" : 0.5 * mm, "tangentPropagation" : true, "allowEdgeOverflow" : false});
        }
    });
